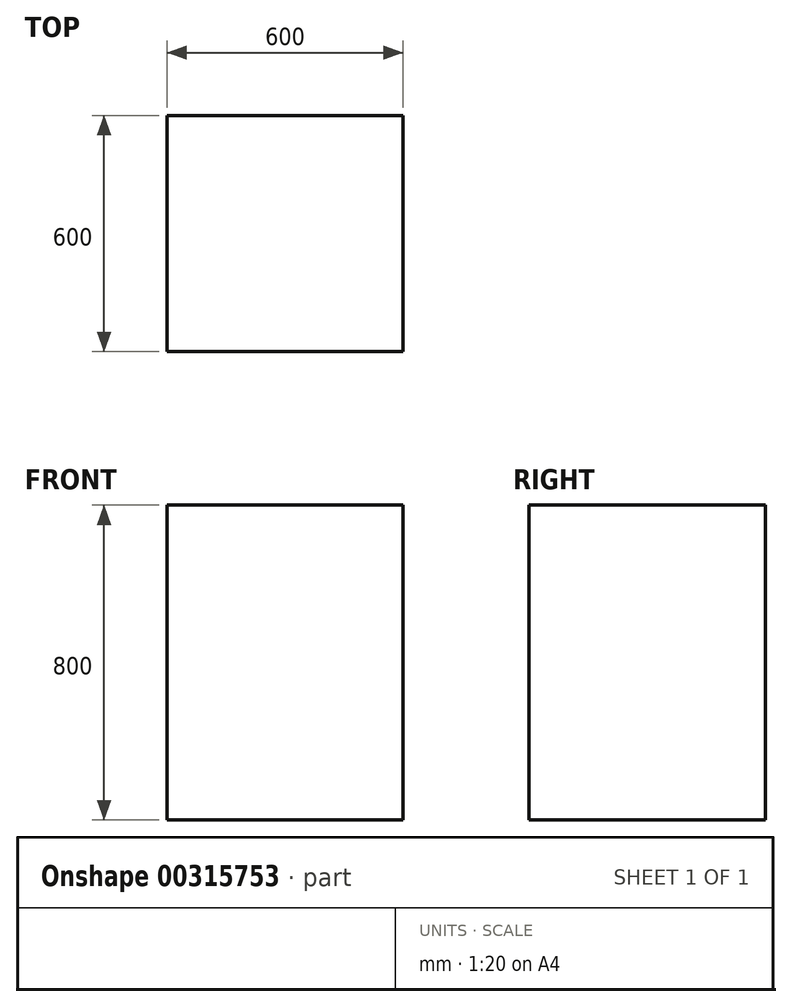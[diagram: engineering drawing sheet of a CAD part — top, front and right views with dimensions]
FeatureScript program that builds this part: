
annotation { "Feature Type Name" : "Feature", "Feature Type Description" : "" }
export const myFeature = defineFeature(function(context is Context, id is Id, definition is map)
    precondition{}
    {
        {
            var Q0;
            Q0=qCreatedBy(makeId("Top.planeOp"),FACE);
            var sketch = newSketch(context, id + "F0", { "sketchPlane" : qUnion([Q0])});
            skLineSegment(sketch, "E0.bottom", {"start": v(0, 0) * mm, "end": v(600, 0) * mm});
            skLineSegment(sketch, "E0.top", {"start": v(0, -600) * mm, "end": v(600, -600) * mm});
            skLineSegment(sketch, "E0.left", {"start": v(0, 0) * mm, "end": v(0, -600) * mm});
            skLineSegment(sketch, "E0.right", {"start": v(600, 0) * mm, "end": v(600, -600) * mm});
            skSolve(sketch);
        }
        {
            var Q0;
            Q0=makeQuery(id+"F0.imprint","IMPRINT",FACE,{"disambiguationData":[TD([[makeQuery(id+"F0.imprint","IMPRINT",EDGE,{"derivedFrom":sQuery(id+"F0.wireOp",EDGE,"E0.bottom")}),-1.0]])]});
            extrude(context, id + "F1", {"entities" : qUnion([Q0]), "depth" : 800 * mm});
        }
    });
